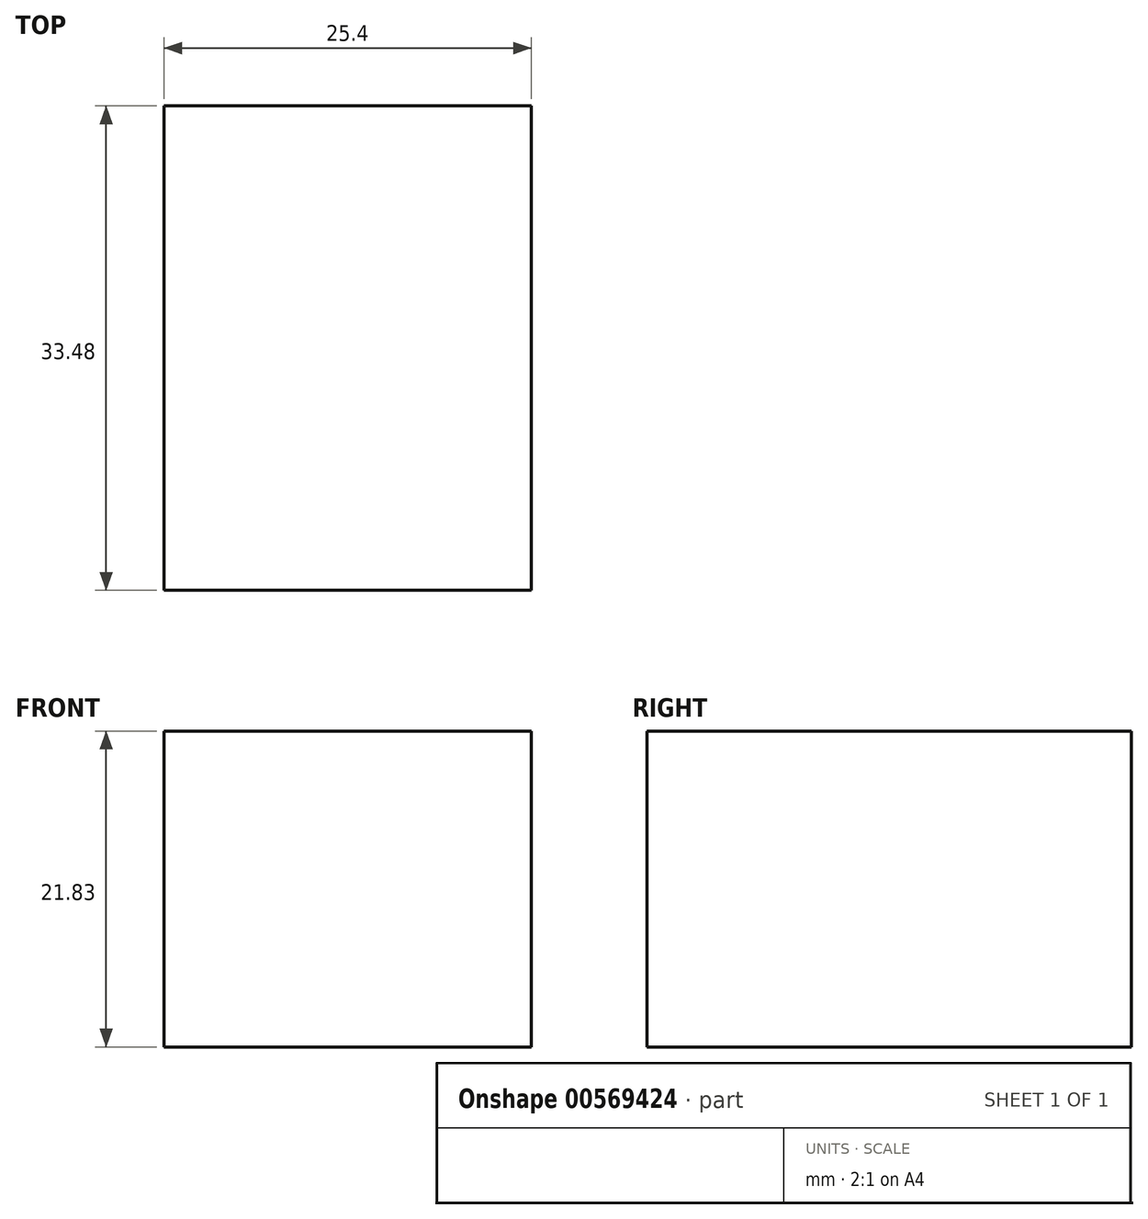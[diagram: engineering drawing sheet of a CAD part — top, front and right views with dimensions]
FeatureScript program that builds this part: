
annotation { "Feature Type Name" : "Feature", "Feature Type Description" : "" }
export const myFeature = defineFeature(function(context is Context, id is Id, definition is map)
    precondition{}
    {
        {
            var Q0;
            Q0=qCreatedBy(makeId("Right.planeOp"),FACE);
            var sketch = newSketch(context, id + "F0", { "sketchPlane" : qUnion([Q0])});
            skLineSegment(sketch, "E0.bottom", {"start": v(-52.86, 47.12) * mm, "end": v(-57.56, 47.12) * mm});
            skLineSegment(sketch, "E0.top", {"start": v(-52.86, 40.31) * mm, "end": v(-57.56, 40.31) * mm});
            skLineSegment(sketch, "E0.left", {"start": v(-52.86, 47.12) * mm, "end": v(-52.86, 40.31) * mm});
            skLineSegment(sketch, "E0.right", {"start": v(-57.56, 47.12) * mm, "end": v(-57.56, 40.31) * mm});
            skLineSegment(sketch, "E1.bottom", {"start": v(-16.45, 29.25) * mm, "end": v(17.03, 29.25) * mm});
            skLineSegment(sketch, "E1.top", {"start": v(-16.45, 7.42) * mm, "end": v(17.03, 7.42) * mm});
            skLineSegment(sketch, "E1.left", {"start": v(-16.45, 29.25) * mm, "end": v(-16.45, 7.42) * mm});
            skLineSegment(sketch, "E1.right", {"start": v(17.03, 29.25) * mm, "end": v(17.03, 7.42) * mm});
            skSolve(sketch);
        }
        {
            var Q0;
            Q0=makeQuery(id+"F0.imprint","IMPRINT",FACE,{"disambiguationData":[TD([[makeQuery(id+"F0.imprint","IMPRINT",EDGE,{"derivedFrom":sQuery(id+"F0.wireOp",EDGE,"E1.bottom")}),-1.0]])]});
            extrude(context, id + "F1", {"entities" : qUnion([Q0]), "depth" : 25.4 * mm, "offsetDistance" : 25.4 * mm});
        }
    });
